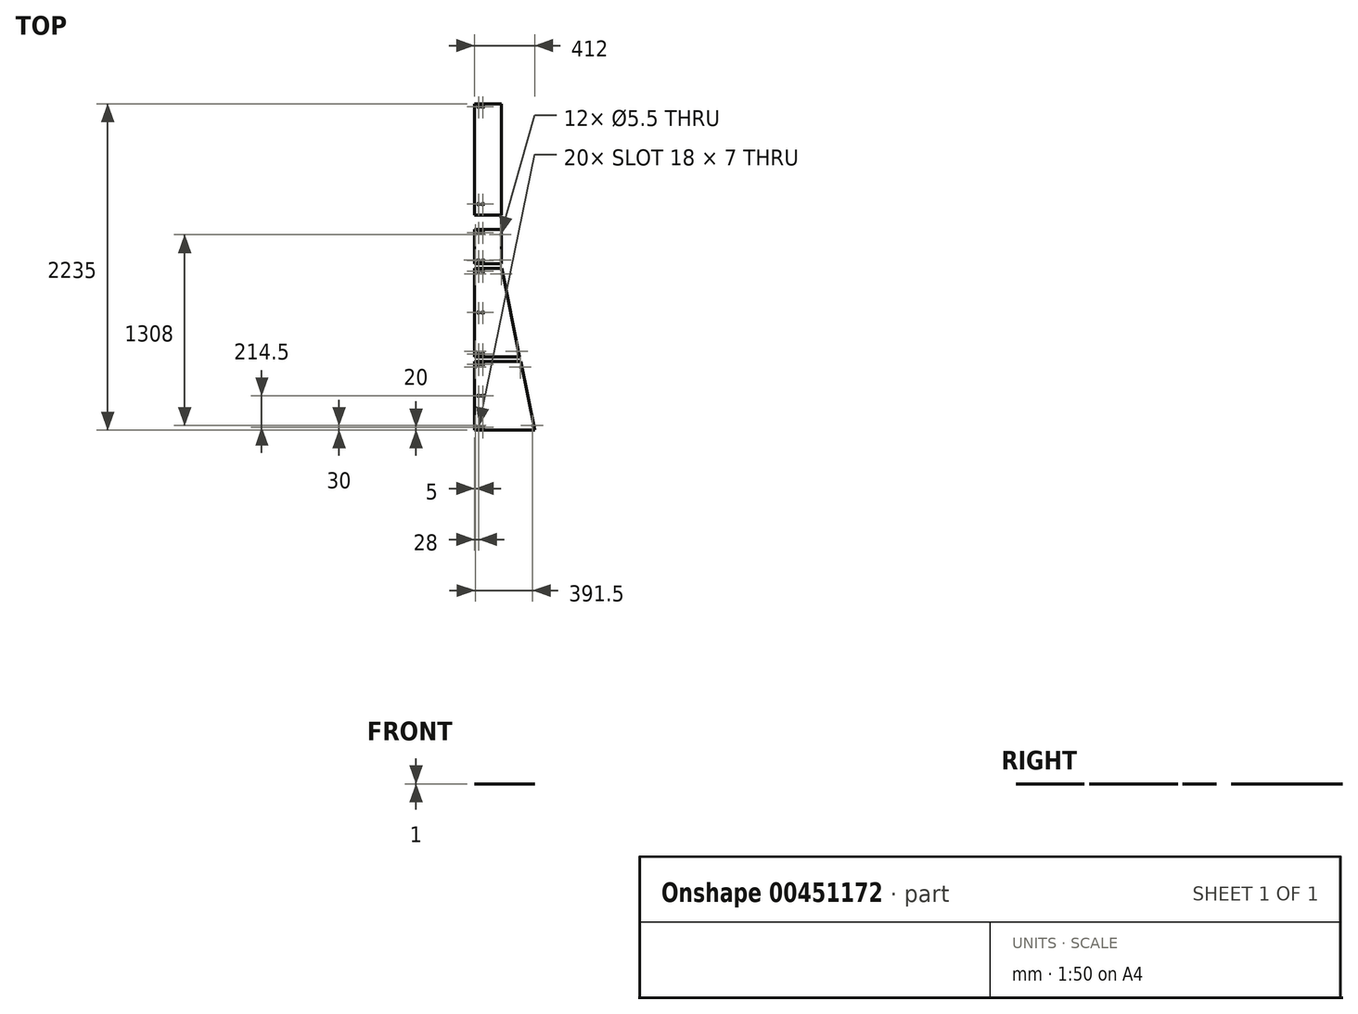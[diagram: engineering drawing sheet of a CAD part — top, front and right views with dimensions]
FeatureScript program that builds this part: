
annotation { "Feature Type Name" : "Feature", "Feature Type Description" : "" }
export const myFeature = defineFeature(function(context is Context, id is Id, definition is map)
    precondition{}
    {
        {
            var Q0;
            Q0=qCreatedBy(makeId("Top.planeOp"),FACE);
            var sketch = newSketch(context, id + "F0", { "sketchPlane" : qUnion([Q0])});
            skLineSegment(sketch, "E0", {"start": v(0, 0) * mm, "end": v(0, 469) * mm});
            skLineSegment(sketch, "E1", {"start": v(0, 469) * mm, "end": v(317.37, 469) * mm});
            skLineSegment(sketch, "E2", {"start": v(317.37, 469) * mm, "end": v(412, 0) * mm});
            skLineSegment(sketch, "E3", {"start": v(412, 0) * mm, "end": v(0, 0) * mm});
            skCircle(sketch, "E4", {"center": v(6.5, 30) * mm, "radius": 2.75 * mm});
            skCircle(sketch, "E5", {"center": v(6.5, 430) * mm, "radius": 2.75 * mm});
            skCircle(sketch, "E6", {"center": v(396.5, 30) * mm, "radius": 2.75 * mm});
            skCircle(sketch, "E7", {"center": v(315.85, 430) * mm, "radius": 2.75 * mm});
            skLineSegment(sketch, "E8.bottom", {"start": v(31.5, 443.5) * mm, "end": v(24.5, 443.5) * mm, "construction": true});
            skLineSegment(sketch, "E8.top", {"start": v(31.5, 454.5) * mm, "end": v(24.5, 454.5) * mm, "construction": true});
            skLineSegment(sketch, "E8.left", {"start": v(31.5, 443.5) * mm, "end": v(31.5, 454.5) * mm});
            skLineSegment(sketch, "E8.right", {"start": v(24.5, 443.5) * mm, "end": v(24.5, 454.5) * mm});
            skPoint(sketch, "E8.middle", {"position": v(28, 449) * mm});
            skArc(sketch, "E9", {"start": v(31.5, 454.5) * mm, "mid": v(28, 458) * mm, "end": v(24.5, 454.5) * mm});
            skArc(sketch, "E10", {"start": v(24.5, 443.5) * mm, "mid": v(28, 440) * mm, "end": v(31.5, 443.5) * mm});
            skLineSegment(sketch, "E11.bottom", {"start": v(61.5, 443.5) * mm, "end": v(54.5, 443.5) * mm, "construction": true});
            skLineSegment(sketch, "E11.top", {"start": v(61.5, 454.5) * mm, "end": v(54.5, 454.5) * mm, "construction": true});
            skLineSegment(sketch, "E11.left", {"start": v(61.5, 443.5) * mm, "end": v(61.5, 454.5) * mm});
            skLineSegment(sketch, "E11.right", {"start": v(54.5, 443.5) * mm, "end": v(54.5, 454.5) * mm});
            skPoint(sketch, "E11.middle", {"position": v(58, 449) * mm});
            skArc(sketch, "E12", {"start": v(61.5, 454.5) * mm, "mid": v(58, 458) * mm, "end": v(54.5, 454.5) * mm});
            skArc(sketch, "E13", {"start": v(54.5, 443.5) * mm, "mid": v(58, 440) * mm, "end": v(61.5, 443.5) * mm});
            skLineSegment(sketch, "E14.bottom", {"start": v(31.5, 14.5) * mm, "end": v(24.5, 14.5) * mm, "construction": true});
            skLineSegment(sketch, "E14.top", {"start": v(31.5, 25.5) * mm, "end": v(24.5, 25.5) * mm, "construction": true});
            skLineSegment(sketch, "E14.left", {"start": v(31.5, 14.5) * mm, "end": v(31.5, 25.5) * mm});
            skLineSegment(sketch, "E14.right", {"start": v(24.5, 14.5) * mm, "end": v(24.5, 25.5) * mm});
            skPoint(sketch, "E14.middle", {"position": v(28, 20) * mm});
            skArc(sketch, "E15", {"start": v(31.5, 25.5) * mm, "mid": v(28, 29) * mm, "end": v(24.5, 25.5) * mm});
            skArc(sketch, "E16", {"start": v(24.5, 14.5) * mm, "mid": v(28, 11) * mm, "end": v(31.5, 14.5) * mm});
            skLineSegment(sketch, "E17.bottom", {"start": v(61.5, 14.5) * mm, "end": v(54.5, 14.5) * mm, "construction": true});
            skLineSegment(sketch, "E17.top", {"start": v(61.5, 25.5) * mm, "end": v(54.5, 25.5) * mm, "construction": true});
            skLineSegment(sketch, "E17.left", {"start": v(61.5, 14.5) * mm, "end": v(61.5, 25.5) * mm});
            skLineSegment(sketch, "E17.right", {"start": v(54.5, 14.5) * mm, "end": v(54.5, 25.5) * mm});
            skPoint(sketch, "E17.middle", {"position": v(58, 20) * mm});
            skArc(sketch, "E18", {"start": v(61.5, 25.5) * mm, "mid": v(58, 29) * mm, "end": v(54.5, 25.5) * mm});
            skArc(sketch, "E19", {"start": v(54.5, 14.5) * mm, "mid": v(58, 11) * mm, "end": v(61.5, 14.5) * mm});
            skLineSegment(sketch, "E20", {"start": v(0, 501) * mm, "end": v(309, 501) * mm});
            skLineSegment(sketch, "E21", {"start": v(309, 501) * mm, "end": v(186.33, 1109) * mm});
            skLineSegment(sketch, "E22", {"start": v(186.33, 1109) * mm, "end": v(0, 1109) * mm});
            skLineSegment(sketch, "E23", {"start": v(0, 1109) * mm, "end": v(0, 501) * mm});
            skPoint(sketch, "E24", {"position": v(0, 805) * mm});
            skCircle(sketch, "E25", {"center": v(6.5, 540) * mm, "radius": 2.75 * mm});
            skCircle(sketch, "E26", {"center": v(6.5, 1070) * mm, "radius": 2.75 * mm});
            skCircle(sketch, "E27", {"center": v(184.7, 1070) * mm, "radius": 2.75 * mm});
            skCircle(sketch, "E28", {"center": v(291.63, 540) * mm, "radius": 2.75 * mm});
            skLineSegment(sketch, "E29.bottom", {"start": v(0, 1141) * mm, "end": v(183, 1141) * mm});
            skLineSegment(sketch, "E29.top", {"start": v(0, 1373) * mm, "end": v(183, 1373) * mm});
            skLineSegment(sketch, "E29.left", {"start": v(0, 1141) * mm, "end": v(0, 1373) * mm});
            skLineSegment(sketch, "E29.right", {"start": v(183, 1141) * mm, "end": v(183, 1373) * mm});
            skCircle(sketch, "E30", {"center": v(5, 1165) * mm, "radius": 2.75 * mm});
            skCircle(sketch, "E31", {"center": v(178, 1165) * mm, "radius": 2.75 * mm});
            skCircle(sketch, "E32", {"center": v(5, 1338) * mm, "radius": 2.75 * mm});
            skCircle(sketch, "E33", {"center": v(178, 1338) * mm, "radius": 2.75 * mm});
            skLineSegment(sketch, "E34.bottom", {"start": v(31.5, 1347.5) * mm, "end": v(24.5, 1347.5) * mm, "construction": true});
            skLineSegment(sketch, "E34.top", {"start": v(31.5, 1358.5) * mm, "end": v(24.5, 1358.5) * mm, "construction": true});
            skLineSegment(sketch, "E34.left", {"start": v(31.5, 1347.5) * mm, "end": v(31.5, 1358.5) * mm});
            skLineSegment(sketch, "E34.right", {"start": v(24.5, 1347.5) * mm, "end": v(24.5, 1358.5) * mm});
            skPoint(sketch, "E34.middle", {"position": v(28, 1353) * mm});
            skArc(sketch, "E35", {"start": v(31.5, 1358.5) * mm, "mid": v(28, 1362) * mm, "end": v(24.5, 1358.5) * mm});
            skArc(sketch, "E36", {"start": v(24.5, 1347.5) * mm, "mid": v(28, 1344) * mm, "end": v(31.5, 1347.5) * mm});
            skLineSegment(sketch, "E37.bottom", {"start": v(61.5, 1347.5) * mm, "end": v(54.5, 1347.5) * mm, "construction": true});
            skLineSegment(sketch, "E37.top", {"start": v(61.5, 1358.5) * mm, "end": v(54.5, 1358.5) * mm, "construction": true});
            skLineSegment(sketch, "E37.left", {"start": v(61.5, 1347.5) * mm, "end": v(61.5, 1358.5) * mm});
            skLineSegment(sketch, "E37.right", {"start": v(54.5, 1347.5) * mm, "end": v(54.5, 1358.5) * mm});
            skPoint(sketch, "E37.middle", {"position": v(58, 1353) * mm});
            skArc(sketch, "E38", {"start": v(61.5, 1358.5) * mm, "mid": v(58, 1362) * mm, "end": v(54.5, 1358.5) * mm});
            skArc(sketch, "E39", {"start": v(54.5, 1347.5) * mm, "mid": v(58, 1344) * mm, "end": v(61.5, 1347.5) * mm});
            skLineSegment(sketch, "E40.bottom", {"start": v(31.5, 1155.5) * mm, "end": v(24.5, 1155.5) * mm, "construction": true});
            skLineSegment(sketch, "E40.top", {"start": v(31.5, 1166.5) * mm, "end": v(24.5, 1166.5) * mm, "construction": true});
            skLineSegment(sketch, "E40.left", {"start": v(31.5, 1155.5) * mm, "end": v(31.5, 1166.5) * mm});
            skLineSegment(sketch, "E40.right", {"start": v(24.5, 1155.5) * mm, "end": v(24.5, 1166.5) * mm});
            skPoint(sketch, "E40.middle", {"position": v(28, 1161) * mm});
            skArc(sketch, "E41", {"start": v(31.5, 1166.5) * mm, "mid": v(28, 1170) * mm, "end": v(24.5, 1166.5) * mm});
            skArc(sketch, "E42", {"start": v(24.5, 1155.5) * mm, "mid": v(28, 1152) * mm, "end": v(31.5, 1155.5) * mm});
            skLineSegment(sketch, "E43.bottom", {"start": v(61.5, 1155.5) * mm, "end": v(54.5, 1155.5) * mm, "construction": true});
            skLineSegment(sketch, "E43.top", {"start": v(61.5, 1166.5) * mm, "end": v(54.5, 1166.5) * mm, "construction": true});
            skLineSegment(sketch, "E43.left", {"start": v(61.5, 1155.5) * mm, "end": v(61.5, 1166.5) * mm});
            skLineSegment(sketch, "E43.right", {"start": v(54.5, 1155.5) * mm, "end": v(54.5, 1166.5) * mm});
            skPoint(sketch, "E43.middle", {"position": v(58, 1161) * mm});
            skArc(sketch, "E44", {"start": v(61.5, 1166.5) * mm, "mid": v(58, 1170) * mm, "end": v(54.5, 1166.5) * mm});
            skArc(sketch, "E45", {"start": v(54.5, 1155.5) * mm, "mid": v(58, 1152) * mm, "end": v(61.5, 1155.5) * mm});
            skLineSegment(sketch, "E46.bottom", {"start": v(31.5, 515.5) * mm, "end": v(24.5, 515.5) * mm, "construction": true});
            skLineSegment(sketch, "E46.top", {"start": v(31.5, 526.5) * mm, "end": v(24.5, 526.5) * mm, "construction": true});
            skLineSegment(sketch, "E46.left", {"start": v(31.5, 515.5) * mm, "end": v(31.5, 526.5) * mm});
            skLineSegment(sketch, "E46.right", {"start": v(24.5, 515.5) * mm, "end": v(24.5, 526.5) * mm});
            skPoint(sketch, "E46.middle", {"position": v(28, 521) * mm});
            skArc(sketch, "E47", {"start": v(31.5, 526.5) * mm, "mid": v(28, 530) * mm, "end": v(24.5, 526.5) * mm});
            skArc(sketch, "E48", {"start": v(24.5, 515.5) * mm, "mid": v(28, 512) * mm, "end": v(31.5, 515.5) * mm});
            skLineSegment(sketch, "E49.bottom", {"start": v(61.5, 515.5) * mm, "end": v(54.5, 515.5) * mm, "construction": true});
            skLineSegment(sketch, "E49.top", {"start": v(61.5, 526.5) * mm, "end": v(54.5, 526.5) * mm, "construction": true});
            skLineSegment(sketch, "E49.left", {"start": v(61.5, 515.5) * mm, "end": v(61.5, 526.5) * mm});
            skLineSegment(sketch, "E49.right", {"start": v(54.5, 515.5) * mm, "end": v(54.5, 526.5) * mm});
            skPoint(sketch, "E49.middle", {"position": v(58, 521) * mm});
            skArc(sketch, "E50", {"start": v(61.5, 526.5) * mm, "mid": v(58, 530) * mm, "end": v(54.5, 526.5) * mm});
            skArc(sketch, "E51", {"start": v(54.5, 515.5) * mm, "mid": v(58, 512) * mm, "end": v(61.5, 515.5) * mm});
            skLineSegment(sketch, "E52.bottom", {"start": v(31.5, 1083.5) * mm, "end": v(24.5, 1083.5) * mm, "construction": true});
            skLineSegment(sketch, "E52.top", {"start": v(31.5, 1094.5) * mm, "end": v(24.5, 1094.5) * mm, "construction": true});
            skLineSegment(sketch, "E52.left", {"start": v(31.5, 1083.5) * mm, "end": v(31.5, 1094.5) * mm});
            skLineSegment(sketch, "E52.right", {"start": v(24.5, 1083.5) * mm, "end": v(24.5, 1094.5) * mm});
            skPoint(sketch, "E52.middle", {"position": v(28, 1089) * mm});
            skArc(sketch, "E53", {"start": v(31.5, 1094.5) * mm, "mid": v(28, 1098) * mm, "end": v(24.5, 1094.5) * mm});
            skArc(sketch, "E54", {"start": v(24.5, 1083.5) * mm, "mid": v(28, 1080) * mm, "end": v(31.5, 1083.5) * mm});
            skLineSegment(sketch, "E55.bottom", {"start": v(61.5, 1083.5) * mm, "end": v(54.5, 1083.5) * mm, "construction": true});
            skLineSegment(sketch, "E55.top", {"start": v(61.5, 1094.5) * mm, "end": v(54.5, 1094.5) * mm, "construction": true});
            skLineSegment(sketch, "E55.left", {"start": v(61.5, 1083.5) * mm, "end": v(61.5, 1094.5) * mm});
            skLineSegment(sketch, "E55.right", {"start": v(54.5, 1083.5) * mm, "end": v(54.5, 1094.5) * mm});
            skPoint(sketch, "E55.middle", {"position": v(58, 1089) * mm});
            skArc(sketch, "E56", {"start": v(61.5, 1094.5) * mm, "mid": v(58, 1098) * mm, "end": v(54.5, 1094.5) * mm});
            skArc(sketch, "E57", {"start": v(54.5, 1083.5) * mm, "mid": v(58, 1080) * mm, "end": v(61.5, 1083.5) * mm});
            skLineSegment(sketch, "E58.bottom", {"start": v(31.5, 799.5) * mm, "end": v(24.5, 799.5) * mm, "construction": true});
            skLineSegment(sketch, "E58.top", {"start": v(31.5, 810.5) * mm, "end": v(24.5, 810.5) * mm, "construction": true});
            skLineSegment(sketch, "E58.left", {"start": v(31.5, 799.5) * mm, "end": v(31.5, 810.5) * mm});
            skLineSegment(sketch, "E58.right", {"start": v(24.5, 799.5) * mm, "end": v(24.5, 810.5) * mm});
            skPoint(sketch, "E58.middle", {"position": v(28, 805) * mm});
            skArc(sketch, "E59", {"start": v(31.5, 810.5) * mm, "mid": v(28, 814) * mm, "end": v(24.5, 810.5) * mm});
            skArc(sketch, "E60", {"start": v(24.5, 799.5) * mm, "mid": v(28, 796) * mm, "end": v(31.5, 799.5) * mm});
            skLineSegment(sketch, "E61.bottom", {"start": v(61.5, 799.5) * mm, "end": v(54.5, 799.5) * mm, "construction": true});
            skLineSegment(sketch, "E61.top", {"start": v(61.5, 810.5) * mm, "end": v(54.5, 810.5) * mm, "construction": true});
            skLineSegment(sketch, "E61.left", {"start": v(61.5, 799.5) * mm, "end": v(61.5, 810.5) * mm});
            skLineSegment(sketch, "E61.right", {"start": v(54.5, 799.5) * mm, "end": v(54.5, 810.5) * mm});
            skPoint(sketch, "E61.middle", {"position": v(58, 805) * mm});
            skArc(sketch, "E62", {"start": v(61.5, 810.5) * mm, "mid": v(58, 814) * mm, "end": v(54.5, 810.5) * mm});
            skArc(sketch, "E63", {"start": v(54.5, 799.5) * mm, "mid": v(58, 796) * mm, "end": v(61.5, 799.5) * mm});
            skLineSegment(sketch, "E64.bottom", {"start": v(31.5, 229) * mm, "end": v(24.5, 229) * mm, "construction": true});
            skLineSegment(sketch, "E64.top", {"start": v(31.5, 240) * mm, "end": v(24.5, 240) * mm, "construction": true});
            skLineSegment(sketch, "E64.left", {"start": v(31.5, 229) * mm, "end": v(31.5, 240) * mm});
            skLineSegment(sketch, "E64.right", {"start": v(24.5, 229) * mm, "end": v(24.5, 240) * mm});
            skPoint(sketch, "E64.middle", {"position": v(28, 234.5) * mm});
            skArc(sketch, "E65", {"start": v(31.5, 240) * mm, "mid": v(28, 243.5) * mm, "end": v(24.5, 240) * mm});
            skArc(sketch, "E66", {"start": v(24.5, 229) * mm, "mid": v(28, 225.5) * mm, "end": v(31.5, 229) * mm});
            skLineSegment(sketch, "E67.bottom", {"start": v(61.5, 229) * mm, "end": v(54.5, 229) * mm, "construction": true});
            skLineSegment(sketch, "E67.top", {"start": v(61.5, 240) * mm, "end": v(54.5, 240) * mm, "construction": true});
            skLineSegment(sketch, "E67.left", {"start": v(61.5, 229) * mm, "end": v(61.5, 240) * mm});
            skLineSegment(sketch, "E67.right", {"start": v(54.5, 229) * mm, "end": v(54.5, 240) * mm});
            skPoint(sketch, "E67.middle", {"position": v(58, 234.5) * mm});
            skArc(sketch, "E68", {"start": v(61.5, 240) * mm, "mid": v(58, 243.5) * mm, "end": v(54.5, 240) * mm});
            skArc(sketch, "E69", {"start": v(54.5, 229) * mm, "mid": v(58, 225.5) * mm, "end": v(61.5, 229) * mm});
            skPoint(sketch, "E70", {"position": v(0, 234.5) * mm});
            skLineSegment(sketch, "E71.bottom", {"start": v(0, 1473) * mm, "end": v(183, 1473) * mm});
            skLineSegment(sketch, "E71.top", {"start": v(0, 2235) * mm, "end": v(183, 2235) * mm});
            skLineSegment(sketch, "E71.left", {"start": v(0, 1473) * mm, "end": v(0, 2235) * mm});
            skLineSegment(sketch, "E71.right", {"start": v(183, 1473) * mm, "end": v(183, 2235) * mm});
            skLineSegment(sketch, "E72.bottom", {"start": v(31.5, 1542.5) * mm, "end": v(24.5, 1542.5) * mm, "construction": true});
            skLineSegment(sketch, "E72.top", {"start": v(31.5, 1553.5) * mm, "end": v(24.5, 1553.5) * mm, "construction": true});
            skLineSegment(sketch, "E72.left", {"start": v(31.5, 1542.5) * mm, "end": v(31.5, 1553.5) * mm});
            skLineSegment(sketch, "E72.right", {"start": v(24.5, 1542.5) * mm, "end": v(24.5, 1553.5) * mm});
            skPoint(sketch, "E72.middle", {"position": v(28, 1548) * mm});
            skArc(sketch, "E73", {"start": v(31.5, 1553.5) * mm, "mid": v(28, 1557) * mm, "end": v(24.5, 1553.5) * mm});
            skArc(sketch, "E74", {"start": v(24.5, 1542.5) * mm, "mid": v(28, 1539) * mm, "end": v(31.5, 1542.5) * mm});
            skLineSegment(sketch, "E75.bottom", {"start": v(61.5, 1542.5) * mm, "end": v(54.5, 1542.5) * mm, "construction": true});
            skLineSegment(sketch, "E75.top", {"start": v(61.5, 1553.5) * mm, "end": v(54.5, 1553.5) * mm, "construction": true});
            skLineSegment(sketch, "E75.left", {"start": v(61.5, 1542.5) * mm, "end": v(61.5, 1553.5) * mm});
            skLineSegment(sketch, "E75.right", {"start": v(54.5, 1542.5) * mm, "end": v(54.5, 1553.5) * mm});
            skPoint(sketch, "E75.middle", {"position": v(58, 1548) * mm});
            skArc(sketch, "E76", {"start": v(61.5, 1553.5) * mm, "mid": v(58, 1557) * mm, "end": v(54.5, 1553.5) * mm});
            skArc(sketch, "E77", {"start": v(54.5, 1542.5) * mm, "mid": v(58, 1539) * mm, "end": v(61.5, 1542.5) * mm});
            skLineSegment(sketch, "E78", {"start": v(19.16, 1533) * mm, "end": v(75.88, 1533) * mm, "construction": true});
            skLineSegment(sketch, "E79.bottom", {"start": v(31.5, 2209.5) * mm, "end": v(24.5, 2209.5) * mm, "construction": true});
            skLineSegment(sketch, "E79.top", {"start": v(31.5, 2220.5) * mm, "end": v(24.5, 2220.5) * mm, "construction": true});
            skLineSegment(sketch, "E79.left", {"start": v(31.5, 2209.5) * mm, "end": v(31.5, 2220.5) * mm});
            skLineSegment(sketch, "E79.right", {"start": v(24.5, 2209.5) * mm, "end": v(24.5, 2220.5) * mm});
            skPoint(sketch, "E79.middle", {"position": v(28, 2215) * mm});
            skArc(sketch, "E80", {"start": v(31.5, 2220.5) * mm, "mid": v(28, 2224) * mm, "end": v(24.5, 2220.5) * mm});
            skArc(sketch, "E81", {"start": v(24.5, 2209.5) * mm, "mid": v(28, 2206) * mm, "end": v(31.5, 2209.5) * mm});
            skLineSegment(sketch, "E82.bottom", {"start": v(61.5, 2209.5) * mm, "end": v(54.5, 2209.5) * mm, "construction": true});
            skLineSegment(sketch, "E82.top", {"start": v(61.5, 2220.5) * mm, "end": v(54.5, 2220.5) * mm, "construction": true});
            skLineSegment(sketch, "E82.left", {"start": v(61.5, 2209.5) * mm, "end": v(61.5, 2220.5) * mm});
            skLineSegment(sketch, "E82.right", {"start": v(54.5, 2209.5) * mm, "end": v(54.5, 2220.5) * mm});
            skPoint(sketch, "E82.middle", {"position": v(58, 2215) * mm});
            skArc(sketch, "E83", {"start": v(61.5, 2220.5) * mm, "mid": v(58, 2224) * mm, "end": v(54.5, 2220.5) * mm});
            skArc(sketch, "E84", {"start": v(54.5, 2209.5) * mm, "mid": v(58, 2206) * mm, "end": v(61.5, 2209.5) * mm});
            skSolve(sketch);
        }
        {
            var Q0;
            Q0 = qSketchRegion(id + "F0", true);
            extrude(context, id + "F1", {"entities" : qUnion([Q0]), "depth" : 1 * mm, "offsetDistance" : 25 * mm});
        }
    });
